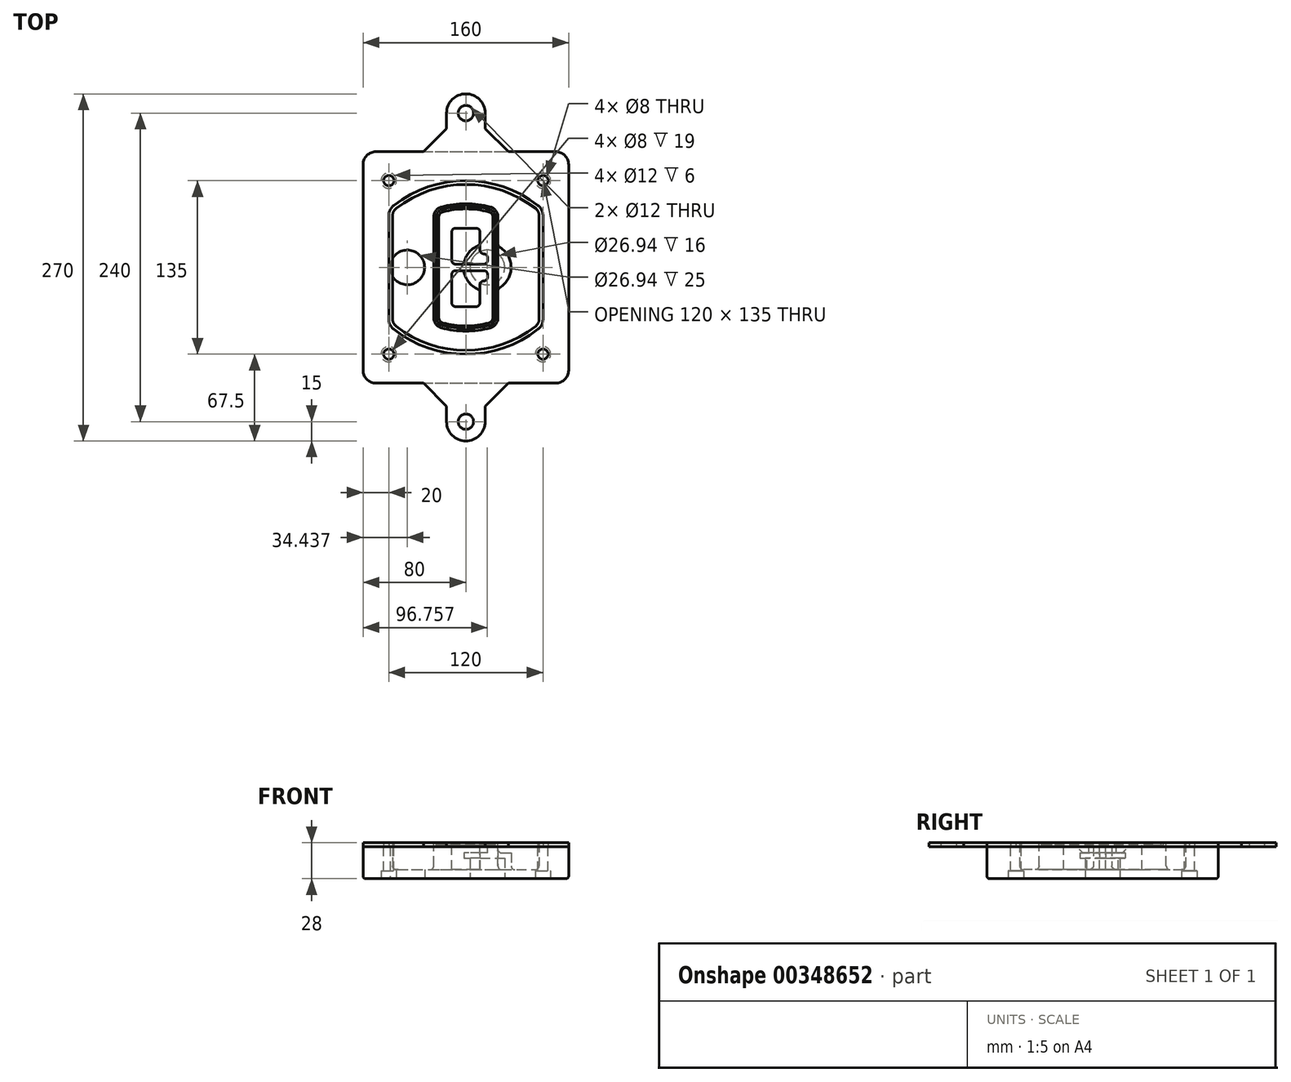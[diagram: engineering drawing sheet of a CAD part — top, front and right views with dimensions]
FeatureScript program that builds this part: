
annotation { "Feature Type Name" : "Feature", "Feature Type Description" : "" }
export const myFeature = defineFeature(function(context is Context, id is Id, definition is map)
    precondition{}
    {
        {
            var Q0;
            Q0=qCreatedBy(makeId("Top.planeOp"),FACE);
            var sketch = newSketch(context, id + "F0", { "sketchPlane" : qUnion([Q0])});
            skPoint(sketch, "E0.rect.middle", {"position": v(0, 0) * mm});
            skLineSegment(sketch, "E1.bottom", {"start": v(-70, -90) * mm, "end": v(70, -90) * mm});
            skLineSegment(sketch, "E1.top", {"start": v(-70, 90) * mm, "end": v(70, 90) * mm});
            skLineSegment(sketch, "E1.left", {"start": v(-80, -80) * mm, "end": v(-80, 80) * mm});
            skLineSegment(sketch, "E1.right", {"start": v(80, -80) * mm, "end": v(80, 80) * mm});
            skLineSegment(sketch, "E2", {"start": v(-80, 90) * mm, "end": v(80, -90) * mm, "construction": true});
            skLineSegment(sketch, "E3", {"start": v(80, 90) * mm, "end": v(-80, -90) * mm, "construction": true});
            skCircle(sketch, "E4", {"center": v(-60, 67.5) * mm, "radius": 4 * mm});
            skCircle(sketch, "E5", {"center": v(60, 67.5) * mm, "radius": 4 * mm});
            skCircle(sketch, "E6", {"center": v(60, -67.5) * mm, "radius": 4 * mm});
            skCircle(sketch, "E7", {"center": v(-60, -67.5) * mm, "radius": 4 * mm});
            skLineSegment(sketch, "E8", {"start": v(-60, 67.5) * mm, "end": v(60, 67.5) * mm, "construction": true});
            skLineSegment(sketch, "E9", {"start": v(60, 67.5) * mm, "end": v(60, -67.5) * mm, "construction": true});
            skLineSegment(sketch, "E10", {"start": v(60, -67.5) * mm, "end": v(-60, -67.5) * mm, "construction": true});
            skLineSegment(sketch, "E11", {"start": v(-60, -67.5) * mm, "end": v(-60, 67.5) * mm, "construction": true});
            skLineSegment(sketch, "E12", {"start": v(-60, 40.3) * mm, "end": v(-60, -40.3) * mm});
            skLineSegment(sketch, "E13", {"start": v(60, 40.3) * mm, "end": v(60, -40.3) * mm});
            skArc(sketch, "E14", {"start": v(56.15, 48.18) * mm, "mid": v(0, 67.5) * mm, "end": v(-56.15, 48.18) * mm});
            skArc(sketch, "E15", {"start": v(-56.15, -48.18) * mm, "mid": v(0, -67.5) * mm, "end": v(56.15, -48.18) * mm});
            skLineSegment(sketch, "E16", {"start": v(-60, 0) * mm, "end": v(60, 0) * mm, "construction": true});
            skPoint(sketch, "E17.visualSharp", {"position": v(-60, -45) * mm});
            skArc(sketch, "E17.filletArc", {"start": v(-60, -40.3) * mm, "mid": v(-58.99, -44.68) * mm, "end": v(-56.15, -48.18) * mm});
            skPoint(sketch, "E18.visualSharp", {"position": v(-60, 45) * mm});
            skArc(sketch, "E18.filletArc", {"start": v(-56.15, 48.18) * mm, "mid": v(-58.99, 44.68) * mm, "end": v(-60, 40.3) * mm});
            skPoint(sketch, "E19.visualSharp", {"position": v(60, 45) * mm});
            skArc(sketch, "E19.filletArc", {"start": v(60, 40.3) * mm, "mid": v(58.99, 44.68) * mm, "end": v(56.15, 48.18) * mm});
            skPoint(sketch, "E20.visualSharp", {"position": v(60, -45) * mm});
            skArc(sketch, "E20.filletArc", {"start": v(56.15, -48.18) * mm, "mid": v(58.99, -44.68) * mm, "end": v(60, -40.3) * mm});
            skPoint(sketch, "E21.visualSharp", {"position": v(-80, 90) * mm});
            skArc(sketch, "E21.filletArc", {"start": v(-70, 90) * mm, "mid": v(-77.07, 87.07) * mm, "end": v(-80, 80) * mm});
            skPoint(sketch, "E22.visualSharp", {"position": v(80, 90) * mm});
            skArc(sketch, "E22.filletArc", {"start": v(80, 80) * mm, "mid": v(77.07, 87.07) * mm, "end": v(70, 90) * mm});
            skPoint(sketch, "E23.visualSharp", {"position": v(80, -90) * mm});
            skArc(sketch, "E23.filletArc", {"start": v(70, -90) * mm, "mid": v(77.07, -87.07) * mm, "end": v(80, -80) * mm});
            skPoint(sketch, "E24.visualSharp", {"position": v(-80, -90) * mm});
            skArc(sketch, "E24.filletArc", {"start": v(-80, -80) * mm, "mid": v(-77.07, -87.07) * mm, "end": v(-70, -90) * mm});
            skArc(sketch, "E25.0", {"start": v(57, 40.3) * mm, "mid": v(56.3, 43.36) * mm, "end": v(54.3, 45.81) * mm});
            skLineSegment(sketch, "E25.1", {"start": v(57, 40.3) * mm, "end": v(57, -40.3) * mm});
            skArc(sketch, "E25.2", {"start": v(54.3, -45.81) * mm, "mid": v(56.3, -43.36) * mm, "end": v(57, -40.3) * mm});
            skArc(sketch, "E25.3", {"start": v(-54.3, -45.81) * mm, "mid": v(0, -64.5) * mm, "end": v(54.3, -45.81) * mm});
            skArc(sketch, "E25.4", {"start": v(-57, -40.3) * mm, "mid": v(-56.3, -43.36) * mm, "end": v(-54.3, -45.81) * mm});
            skArc(sketch, "E25.5", {"start": v(54.3, 45.81) * mm, "mid": v(0, 64.5) * mm, "end": v(-54.3, 45.81) * mm});
            skLineSegment(sketch, "E25.6", {"start": v(-57, 40.3) * mm, "end": v(-57, -40.3) * mm});
            skArc(sketch, "E25.7", {"start": v(-54.3, 45.81) * mm, "mid": v(-56.3, 43.36) * mm, "end": v(-57, 40.3) * mm});
            skArc(sketch, "E26.0", {"start": v(-58.62, 51.33) * mm, "mid": v(-62.58, 46.43) * mm, "end": v(-64, 40.3) * mm});
            skArc(sketch, "E26.1", {"start": v(58.62, 51.33) * mm, "mid": v(0, 71.5) * mm, "end": v(-58.62, 51.33) * mm});
            skArc(sketch, "E26.2", {"start": v(64, 40.3) * mm, "mid": v(62.58, 46.43) * mm, "end": v(58.62, 51.33) * mm});
            skLineSegment(sketch, "E26.3", {"start": v(64, 40.3) * mm, "end": v(64, -40.3) * mm});
            skArc(sketch, "E26.4", {"start": v(58.62, -51.33) * mm, "mid": v(62.58, -46.43) * mm, "end": v(64, -40.3) * mm});
            skLineSegment(sketch, "E26.5", {"start": v(-64, 40.3) * mm, "end": v(-64, -40.3) * mm});
            skArc(sketch, "E26.6", {"start": v(-58.62, -51.33) * mm, "mid": v(0, -71.5) * mm, "end": v(58.62, -51.33) * mm});
            skArc(sketch, "E26.7", {"start": v(-64, -40.3) * mm, "mid": v(-62.58, -46.43) * mm, "end": v(-58.62, -51.33) * mm});
            skSolve(sketch);
        }
        {
            var Q0;
            Q0=makeQuery(id+"F0.imprint","IMPRINT",FACE,{"disambiguationData":[TD([[makeQuery(id+"F0.imprint","IMPRINT",EDGE,{"derivedFrom":sQuery(id+"F0.wireOp",EDGE,"E1.bottom")}),1.0]])]});
            var Q1;
            Q1=makeQuery(id+"F0.imprint","IMPRINT",FACE,{"disambiguationData":[TD([[makeQuery(id+"F0.imprint","IMPRINT",EDGE,{"derivedFrom":sQuery(id+"F0.wireOp",EDGE,"E12")}),1.0]])]});
            var Q2;
            Q2=makeQuery(id+"F0.imprint","IMPRINT",FACE,{"disambiguationData":[TD([[makeQuery(id+"F0.imprint","IMPRINT",EDGE,{"derivedFrom":sQuery(id+"F0.wireOp",EDGE,"E25.0")}),1.0]])]});
            var Q3;
            Q3=makeQuery(id+"F0.imprint","IMPRINT",FACE,{"disambiguationData":[TD([[makeQuery(id+"F0.imprint","IMPRINT",EDGE,{"derivedFrom":sQuery(id+"F0.wireOp",EDGE,"E12")}),-1.0]])]});
            extrude(context, id + "F1", {"entities" : qUnion([Q0, Q1, Q2, Q3]), "oppositeDirection" : true, "depth" : 25 * mm});
        }
        {
            var Q0;
            Q0=makeQuery(id+"F0.imprint","IMPRINT",FACE,{"disambiguationData":[TD([[makeQuery(id+"F0.imprint","IMPRINT",EDGE,{"derivedFrom":sQuery(id+"F0.wireOp",EDGE,"E12")}),1.0]])]});
            extrude(context, id + "F2", {"entities" : qUnion([Q0]), "operationType" : NewBodyOperationType.ADD, "depth" : 3 * mm});
        }
        {
            var Q0;
            Q0=makeQuery(id+"F0.imprint","IMPRINT",FACE,{"disambiguationData":[TD([[makeQuery(id+"F0.imprint","IMPRINT",EDGE,{"derivedFrom":sQuery(id+"F0.wireOp",EDGE,"E25.0")}),1.0]])]});
            extrude(context, id + "F3", {"entities" : qUnion([Q0]), "operationType" : NewBodyOperationType.REMOVE, "oppositeDirection" : true, "depth" : 18 * mm});
        }
        {
            var Q0;
            Q0=makeQuery(id+"F2.opExtrude","CAP_FACE",FACE,{"disambiguationData":[OSD([sQuery(id+"F0.wireOp",EDGE,"E12"),sQuery(id+"F0.wireOp",EDGE,"E13"),sQuery(id+"F0.wireOp",EDGE,"E14"),sQuery(id+"F0.wireOp",EDGE,"E15"),sQuery(id+"F0.wireOp",EDGE,"E17.filletArc"),sQuery(id+"F0.wireOp",EDGE,"E18.filletArc"),sQuery(id+"F0.wireOp",EDGE,"E19.filletArc"),sQuery(id+"F0.wireOp",EDGE,"E20.filletArc"),sQuery(id+"F0.wireOp",EDGE,"E25.0"),sQuery(id+"F0.wireOp",EDGE,"E25.1"),sQuery(id+"F0.wireOp",EDGE,"E25.2"),sQuery(id+"F0.wireOp",EDGE,"E25.3"),sQuery(id+"F0.wireOp",EDGE,"E25.4"),sQuery(id+"F0.wireOp",EDGE,"E25.5"),sQuery(id+"F0.wireOp",EDGE,"E25.6"),sQuery(id+"F0.wireOp",EDGE,"E25.7")])],"isStart":false});
            var sketch = newSketch(context, id + "F4", { "sketchPlane" : qUnion([Q0])});
            skArc(sketch, "E27.0", {"start": v(-19.08, -46.97) * mm, "mid": v(0, -49.5) * mm, "end": v(19.08, -46.97) * mm});
            skArc(sketch, "E28.0", {"start": v(19.08, 46.97) * mm, "mid": v(0, 49.5) * mm, "end": v(-19.08, 46.97) * mm});
            skLineSegment(sketch, "E29", {"start": v(-25, 39.25) * mm, "end": v(-25, -39.25) * mm});
            skLineSegment(sketch, "E30", {"start": v(25, 39.25) * mm, "end": v(25, -39.25) * mm});
            skLineSegment(sketch, "E31", {"start": v(-25, 45.1) * mm, "end": v(25, 45.1) * mm, "construction": true});
            skLineSegment(sketch, "E32", {"start": v(-25, -45.1) * mm, "end": v(25, -45.1) * mm, "construction": true});
            skPoint(sketch, "E33.visualSharp", {"position": v(-25, 45.1) * mm});
            skArc(sketch, "E33.filletArc", {"start": v(-19.08, 46.97) * mm, "mid": v(-23.35, 44.11) * mm, "end": v(-25, 39.25) * mm});
            skPoint(sketch, "E34.visualSharp", {"position": v(25, 45.1) * mm});
            skArc(sketch, "E34.filletArc", {"start": v(25, 39.25) * mm, "mid": v(23.35, 44.11) * mm, "end": v(19.08, 46.97) * mm});
            skPoint(sketch, "E35.visualSharp", {"position": v(25, -45.1) * mm});
            skArc(sketch, "E35.filletArc", {"start": v(19.08, -46.97) * mm, "mid": v(23.35, -44.11) * mm, "end": v(25, -39.25) * mm});
            skPoint(sketch, "E36.visualSharp", {"position": v(-25, -45.1) * mm});
            skArc(sketch, "E36.filletArc", {"start": v(-25, -39.25) * mm, "mid": v(-23.35, -44.11) * mm, "end": v(-19.08, -46.97) * mm});
            skArc(sketch, "E37.0", {"start": v(54.3, 45.81) * mm, "mid": v(0, 64.5) * mm, "end": v(-54.3, 45.81) * mm});
            skArc(sketch, "E37.1", {"start": v(-54.3, 45.81) * mm, "mid": v(-56.3, 43.36) * mm, "end": v(-57, 40.3) * mm});
            skLineSegment(sketch, "E37.2", {"start": v(-57, 40.3) * mm, "end": v(-57, -40.3) * mm});
            skArc(sketch, "E37.3", {"start": v(-57, -40.3) * mm, "mid": v(-56.3, -43.36) * mm, "end": v(-54.3, -45.81) * mm});
            skArc(sketch, "E37.4", {"start": v(-54.3, -45.81) * mm, "mid": v(0, -64.5) * mm, "end": v(54.3, -45.81) * mm});
            skArc(sketch, "E37.5", {"start": v(54.3, -45.81) * mm, "mid": v(56.3, -43.36) * mm, "end": v(57, -40.3) * mm});
            skLineSegment(sketch, "E37.6", {"start": v(57, 40.3) * mm, "end": v(57, -40.3) * mm});
            skArc(sketch, "E37.7", {"start": v(57, 40.3) * mm, "mid": v(56.3, 43.36) * mm, "end": v(54.3, 45.81) * mm});
            skLineSegment(sketch, "E38.0", {"start": v(23, 39.25) * mm, "end": v(23, -39.25) * mm});
            skArc(sketch, "E38.1", {"start": v(18.56, -45.04) * mm, "mid": v(21.76, -42.9) * mm, "end": v(23, -39.25) * mm});
            skArc(sketch, "E38.2", {"start": v(-18.56, -45.04) * mm, "mid": v(0, -47.5) * mm, "end": v(18.56, -45.04) * mm});
            skArc(sketch, "E38.3", {"start": v(-23, -39.25) * mm, "mid": v(-21.76, -42.9) * mm, "end": v(-18.56, -45.04) * mm});
            skLineSegment(sketch, "E38.4", {"start": v(-23, 39.25) * mm, "end": v(-23, -39.25) * mm});
            skArc(sketch, "E38.5", {"start": v(23, 39.25) * mm, "mid": v(21.76, 42.9) * mm, "end": v(18.56, 45.04) * mm});
            skArc(sketch, "E38.6", {"start": v(-18.56, 45.04) * mm, "mid": v(-21.76, 42.9) * mm, "end": v(-23, 39.25) * mm});
            skArc(sketch, "E38.7", {"start": v(18.56, 45.04) * mm, "mid": v(0, 47.5) * mm, "end": v(-18.56, 45.04) * mm});
            skArc(sketch, "E39.0", {"start": v(21, 39.25) * mm, "mid": v(20.18, 41.68) * mm, "end": v(18.04, 43.1) * mm});
            skLineSegment(sketch, "E39.1", {"start": v(21, 39.25) * mm, "end": v(21, -39.25) * mm});
            skArc(sketch, "E39.2", {"start": v(18.04, -43.1) * mm, "mid": v(20.18, -41.68) * mm, "end": v(21, -39.25) * mm});
            skArc(sketch, "E39.3", {"start": v(-18.04, -43.1) * mm, "mid": v(0, -45.5) * mm, "end": v(18.04, -43.1) * mm});
            skArc(sketch, "E39.4", {"start": v(-21, -39.25) * mm, "mid": v(-20.18, -41.68) * mm, "end": v(-18.04, -43.1) * mm});
            skArc(sketch, "E39.5", {"start": v(18.04, 43.1) * mm, "mid": v(0, 45.5) * mm, "end": v(-18.04, 43.1) * mm});
            skLineSegment(sketch, "E39.6", {"start": v(-21, 39.25) * mm, "end": v(-21, -39.25) * mm});
            skArc(sketch, "E39.7", {"start": v(-18.04, 43.1) * mm, "mid": v(-20.18, 41.68) * mm, "end": v(-21, 39.25) * mm});
            skLineSegment(sketch, "E40", {"start": v(-25, 0) * mm, "end": v(25, 0) * mm, "construction": true});
            skLineSegment(sketch, "E41", {"start": v(-11, 5.5) * mm, "end": v(-11, 27.5) * mm});
            skLineSegment(sketch, "E42", {"start": v(-8, 30.5) * mm, "end": v(8, 30.5) * mm});
            skLineSegment(sketch, "E43", {"start": v(11, 27.5) * mm, "end": v(11, 13.5) * mm});
            skLineSegment(sketch, "E44", {"start": v(14, 10.5) * mm, "end": v(14, 10.5) * mm});
            skLineSegment(sketch, "E45", {"start": v(17, 7.5) * mm, "end": v(17, 5.5) * mm});
            skLineSegment(sketch, "E46", {"start": v(14, 2.5) * mm, "end": v(-8, 2.5) * mm});
            skPoint(sketch, "E47.visualSharp", {"position": v(-11, 30.5) * mm});
            skArc(sketch, "E47.filletArc", {"start": v(-8, 30.5) * mm, "mid": v(-10.12, 29.62) * mm, "end": v(-11, 27.5) * mm});
            skPoint(sketch, "E48.visualSharp", {"position": v(11, 30.5) * mm});
            skArc(sketch, "E48.filletArc", {"start": v(11, 27.5) * mm, "mid": v(10.12, 29.62) * mm, "end": v(8, 30.5) * mm});
            skPoint(sketch, "E49.visualSharp", {"position": v(11, 10.5) * mm});
            skArc(sketch, "E49.filletArc", {"start": v(11, 13.5) * mm, "mid": v(11.88, 11.38) * mm, "end": v(14, 10.5) * mm});
            skPoint(sketch, "E50.visualSharp", {"position": v(17, 10.5) * mm});
            skArc(sketch, "E50.filletArc", {"start": v(17, 7.5) * mm, "mid": v(16.12, 9.62) * mm, "end": v(14, 10.5) * mm});
            skPoint(sketch, "E51.visualSharp", {"position": v(17, 2.5) * mm});
            skArc(sketch, "E51.filletArc", {"start": v(14, 2.5) * mm, "mid": v(16.12, 3.38) * mm, "end": v(17, 5.5) * mm});
            skPoint(sketch, "E52.visualSharp", {"position": v(-11, 2.5) * mm});
            skArc(sketch, "E52.filletArc", {"start": v(-11, 5.5) * mm, "mid": v(-10.12, 3.38) * mm, "end": v(-8, 2.5) * mm});
            skLineSegment(sketch, "E53.0.MirrorCS", {"start": v(14, -2.5) * mm, "end": v(-8, -2.5) * mm});
            skArc(sketch, "E54.0.MirrorCS", {"start": v(-11, -5.5) * mm, "mid": v(-10.12, -3.38) * mm, "end": v(-8, -2.5) * mm});
            skLineSegment(sketch, "E55.0.MirrorCS", {"start": v(-11, -5.5) * mm, "end": v(-11, -27.5) * mm});
            skArc(sketch, "E56.0.MirrorCS", {"start": v(-8, -30.5) * mm, "mid": v(-10.12, -29.62) * mm, "end": v(-11, -27.5) * mm});
            skLineSegment(sketch, "E57.0.MirrorCS", {"start": v(-8, -30.5) * mm, "end": v(8, -30.5) * mm});
            skArc(sketch, "E58.0.MirrorCS", {"start": v(11, -27.5) * mm, "mid": v(10.12, -29.62) * mm, "end": v(8, -30.5) * mm});
            skLineSegment(sketch, "E59.0.MirrorCS", {"start": v(11, -27.5) * mm, "end": v(11, -13.5) * mm});
            skArc(sketch, "E60.0.MirrorCS", {"start": v(11, -13.5) * mm, "mid": v(11.88, -11.38) * mm, "end": v(14, -10.5) * mm});
            skArc(sketch, "E61.0.MirrorCS", {"start": v(17, -7.5) * mm, "mid": v(16.12, -9.62) * mm, "end": v(14, -10.5) * mm});
            skLineSegment(sketch, "E62.0.MirrorCS", {"start": v(17, -7.5) * mm, "end": v(17, -5.5) * mm});
            skArc(sketch, "E63.0.MirrorCS", {"start": v(14, -2.5) * mm, "mid": v(16.12, -3.38) * mm, "end": v(17, -5.5) * mm});
            skSolve(sketch);
        }
        {
            var Q0;
            Q0=makeQuery(id+"F4.imprint","IMPRINT",FACE,{"disambiguationData":[TD([[makeQuery(id+"F4.imprint","IMPRINT",EDGE,{"derivedFrom":sQuery(id+"F4.wireOp",EDGE,"E27.0")}),1.0]])]});
            var Q1;
            Q1=makeQuery(id+"F4.imprint","IMPRINT",FACE,{"disambiguationData":[TD([[makeQuery(id+"F4.imprint","IMPRINT",EDGE,{"derivedFrom":sQuery(id+"F4.wireOp",EDGE,"E38.0")}),-1.0]])]});
            var Q2;
            Q2=makeQuery(id+"F4.imprint","IMPRINT",FACE,{"disambiguationData":[TD([[makeQuery(id+"F4.imprint","IMPRINT",EDGE,{"derivedFrom":sQuery(id+"F4.wireOp",EDGE,"E39.0")}),1.0]])]});
            extrude(context, id + "F5", {"entities" : qUnion([Q0, Q1, Q2]), "operationType" : NewBodyOperationType.ADD, "endBound" : BoundingType.UP_TO_NEXT, "oppositeDirection" : true, "depth" : 25 * mm});
        }
        {
            var Q0;
            Q0=makeQuery(id+"F4.imprint","IMPRINT",FACE,{"disambiguationData":[TD([[makeQuery(id+"F4.imprint","IMPRINT",EDGE,{"derivedFrom":sQuery(id+"F4.wireOp",EDGE,"E38.0")}),-1.0]])]});
            extrude(context, id + "F6", {"entities" : qUnion([Q0]), "operationType" : NewBodyOperationType.REMOVE, "oppositeDirection" : true, "depth" : 2 * mm});
        }
        {
            var Q0;
            Q0=makeQuery(id+"F1.opExtrude","CAP_FACE",FACE,{"disambiguationData":[OSD([sQuery(id+"F0.wireOp",EDGE,"E1.bottom"),sQuery(id+"F0.wireOp",EDGE,"E1.top"),sQuery(id+"F0.wireOp",EDGE,"E1.left"),sQuery(id+"F0.wireOp",EDGE,"E1.right"),sQuery(id+"F0.wireOp",EDGE,"E4"),sQuery(id+"F0.wireOp",EDGE,"E5"),sQuery(id+"F0.wireOp",EDGE,"E6"),sQuery(id+"F0.wireOp",EDGE,"E7"),sQuery(id+"F0.wireOp",EDGE,"E21.filletArc"),sQuery(id+"F0.wireOp",EDGE,"E22.filletArc"),sQuery(id+"F0.wireOp",EDGE,"E23.filletArc"),sQuery(id+"F0.wireOp",EDGE,"E24.filletArc")])],"isStart":false});
            var sketch = newSketch(context, id + "F7", { "sketchPlane" : qUnion([Q0])});
            skCircle(sketch, "E64", {"center": v(16.76, 0) * mm, "radius": 13.47 * mm});
            skCircle(sketch, "E65", {"center": v(-45.56, 0) * mm, "radius": 13.47 * mm});
            skLineSegment(sketch, "E66", {"start": v(80, 0) * mm, "end": v(-80, 0) * mm});
            skCircle(sketch, "E67", {"center": v(16.76, 0) * mm, "radius": 18.47 * mm});
            skCircle(sketch, "E68", {"center": v(60, -67.5) * mm, "radius": 6 * mm});
            skCircle(sketch, "E69", {"center": v(-60, -67.5) * mm, "radius": 6 * mm});
            skCircle(sketch, "E70", {"center": v(-60, 67.5) * mm, "radius": 6 * mm});
            skCircle(sketch, "E71", {"center": v(60, 67.5) * mm, "radius": 6 * mm});
            skSolve(sketch);
        }
        {
            var Q0;
            {var subQ1=sQuery(id+"F7.wireOp",EDGE,"E66");var subQ4=sQuery(id+"F7.wireOp",EDGE,"E64");var subQ6=makeQuery(id+"F7.imprint","INTERSECT",VERTEX,{"disambiguationData":[OD(0.0)],"derivedFrom":[subQ4,subQ1]});Q0=makeQuery(id+"F7.imprint","IMPRINT",FACE,{"disambiguationData":[TD([[makeQuery(id+"F7.imprint","IMPRINT",EDGE,{"disambiguationData":[TD([[subQ6,-1.0]])],"derivedFrom":subQ4}),-1.0]])]});}
            var Q1;
            {var subQ0=sQuery(id+"F7.wireOp",EDGE,"E66");var subQ1=sQuery(id+"F7.wireOp",EDGE,"E64");var subQ3=makeQuery(id+"F7.imprint","INTERSECT",VERTEX,{"disambiguationData":[OD(0.0)],"derivedFrom":[subQ1,subQ0]});Q1=makeQuery(id+"F7.imprint","IMPRINT",FACE,{"disambiguationData":[TD([[makeQuery(id+"F7.imprint","IMPRINT",EDGE,{"disambiguationData":[TD([[subQ3,-1.0]])],"derivedFrom":subQ1}),1.0]])]});}
            var Q2;
            {var subQ0=sQuery(id+"F7.wireOp",EDGE,"E66");var subQ1=sQuery(id+"F7.wireOp",EDGE,"E64");var subQ3=makeQuery(id+"F7.imprint","INTERSECT",VERTEX,{"disambiguationData":[OD(0.0)],"derivedFrom":[subQ1,subQ0]});Q2=makeQuery(id+"F7.imprint","IMPRINT",FACE,{"disambiguationData":[TD([[makeQuery(id+"F7.imprint","IMPRINT",EDGE,{"disambiguationData":[TD([[subQ3,1.0]])],"derivedFrom":subQ1}),1.0]])]});}
            var Q3;
            {var subQ1=sQuery(id+"F7.wireOp",EDGE,"E66");var subQ4=sQuery(id+"F7.wireOp",EDGE,"E64");var subQ6=makeQuery(id+"F7.imprint","INTERSECT",VERTEX,{"disambiguationData":[OD(0.0)],"derivedFrom":[subQ4,subQ1]});Q3=makeQuery(id+"F7.imprint","IMPRINT",FACE,{"disambiguationData":[TD([[makeQuery(id+"F7.imprint","IMPRINT",EDGE,{"disambiguationData":[TD([[subQ6,1.0]])],"derivedFrom":subQ4}),-1.0]])]});}
            extrude(context, id + "F8", {"entities" : qUnion([Q0, Q1, Q2, Q3]), "operationType" : NewBodyOperationType.ADD, "oppositeDirection" : true, "depth" : 20 * mm});
        }
        {
            var Q0;
            {var subQ0=sQuery(id+"F7.wireOp",EDGE,"E66");var subQ1=sQuery(id+"F7.wireOp",EDGE,"E64");var subQ3=makeQuery(id+"F7.imprint","INTERSECT",VERTEX,{"disambiguationData":[OD(0.0)],"derivedFrom":[subQ1,subQ0]});Q0=makeQuery(id+"F7.imprint","IMPRINT",FACE,{"disambiguationData":[TD([[makeQuery(id+"F7.imprint","IMPRINT",EDGE,{"disambiguationData":[TD([[subQ3,-1.0]])],"derivedFrom":subQ1}),1.0]])]});}
            var Q1;
            {var subQ0=sQuery(id+"F7.wireOp",EDGE,"E66");var subQ1=sQuery(id+"F7.wireOp",EDGE,"E64");var subQ3=makeQuery(id+"F7.imprint","INTERSECT",VERTEX,{"disambiguationData":[OD(0.0)],"derivedFrom":[subQ1,subQ0]});Q1=makeQuery(id+"F7.imprint","IMPRINT",FACE,{"disambiguationData":[TD([[makeQuery(id+"F7.imprint","IMPRINT",EDGE,{"disambiguationData":[TD([[subQ3,1.0]])],"derivedFrom":subQ1}),1.0]])]});}
            extrude(context, id + "F9", {"entities" : qUnion([Q0, Q1]), "operationType" : NewBodyOperationType.REMOVE, "oppositeDirection" : true, "depth" : 16 * mm});
        }
        {
            var Q0;
            {var subQ0=sQuery(id+"F7.wireOp",EDGE,"E66");var subQ1=sQuery(id+"F7.wireOp",EDGE,"E65");var subQ3=makeQuery(id+"F7.imprint","INTERSECT",VERTEX,{"disambiguationData":[OD(0.0)],"derivedFrom":[subQ1,subQ0]});Q0=makeQuery(id+"F7.imprint","IMPRINT",FACE,{"disambiguationData":[TD([[makeQuery(id+"F7.imprint","IMPRINT",EDGE,{"disambiguationData":[TD([[subQ3,-1.0]])],"derivedFrom":subQ1}),1.0]])]});}
            var Q1;
            {var subQ0=sQuery(id+"F7.wireOp",EDGE,"E66");var subQ1=sQuery(id+"F7.wireOp",EDGE,"E65");var subQ3=makeQuery(id+"F7.imprint","INTERSECT",VERTEX,{"disambiguationData":[OD(0.0)],"derivedFrom":[subQ1,subQ0]});Q1=makeQuery(id+"F7.imprint","IMPRINT",FACE,{"disambiguationData":[TD([[makeQuery(id+"F7.imprint","IMPRINT",EDGE,{"disambiguationData":[TD([[subQ3,1.0]])],"derivedFrom":subQ1}),1.0]])]});}
            extrude(context, id + "F10", {"entities" : qUnion([Q0, Q1]), "operationType" : NewBodyOperationType.REMOVE, "oppositeDirection" : true, "depth" : 25 * mm});
        }
        {
            var Q0;
            Q0=makeQuery(id+"F7.imprint","IMPRINT",FACE,{"disambiguationData":[TD([[makeQuery(id+"F7.imprint","IMPRINT",EDGE,{"derivedFrom":sQuery(id+"F7.wireOp",EDGE,"E68")}),1.0]])]});
            var Q1;
            Q1=makeQuery(id+"F7.imprint","IMPRINT",FACE,{"disambiguationData":[TD([[makeQuery(id+"F7.imprint","IMPRINT",EDGE,{"derivedFrom":makeQuery(id+"F1.opExtrude","CAP_EDGE",EDGE,{"disambiguationData":[OSD([sQuery(id+"F0.wireOp",EDGE,"E5")])],"isStart":false})}),-1.0]])]});
            var Q2;
            Q2=makeQuery(id+"F7.imprint","IMPRINT",FACE,{"disambiguationData":[TD([[makeQuery(id+"F7.imprint","IMPRINT",EDGE,{"derivedFrom":sQuery(id+"F7.wireOp",EDGE,"E69")}),1.0]])]});
            var Q3;
            Q3=makeQuery(id+"F7.imprint","IMPRINT",FACE,{"disambiguationData":[TD([[makeQuery(id+"F7.imprint","IMPRINT",EDGE,{"derivedFrom":makeQuery(id+"F1.opExtrude","CAP_EDGE",EDGE,{"disambiguationData":[OSD([sQuery(id+"F0.wireOp",EDGE,"E4")])],"isStart":false})}),-1.0]])]});
            var Q4;
            Q4=makeQuery(id+"F7.imprint","IMPRINT",FACE,{"disambiguationData":[TD([[makeQuery(id+"F7.imprint","IMPRINT",EDGE,{"derivedFrom":sQuery(id+"F7.wireOp",EDGE,"E70")}),1.0]])]});
            var Q5;
            Q5=makeQuery(id+"F7.imprint","IMPRINT",FACE,{"disambiguationData":[TD([[makeQuery(id+"F7.imprint","IMPRINT",EDGE,{"derivedFrom":makeQuery(id+"F1.opExtrude","CAP_EDGE",EDGE,{"disambiguationData":[OSD([sQuery(id+"F0.wireOp",EDGE,"E7")])],"isStart":false})}),-1.0]])]});
            var Q6;
            Q6=makeQuery(id+"F7.imprint","IMPRINT",FACE,{"disambiguationData":[TD([[makeQuery(id+"F7.imprint","IMPRINT",EDGE,{"derivedFrom":sQuery(id+"F7.wireOp",EDGE,"E71")}),1.0]])]});
            var Q7;
            Q7=makeQuery(id+"F7.imprint","IMPRINT",FACE,{"disambiguationData":[TD([[makeQuery(id+"F7.imprint","IMPRINT",EDGE,{"derivedFrom":makeQuery(id+"F1.opExtrude","CAP_EDGE",EDGE,{"disambiguationData":[OSD([sQuery(id+"F0.wireOp",EDGE,"E6")])],"isStart":false})}),-1.0]])]});
            extrude(context, id + "F11", {"entities" : qUnion([Q0, Q1, Q2, Q3, Q4, Q5, Q6, Q7]), "operationType" : NewBodyOperationType.REMOVE, "oppositeDirection" : true, "depth" : 6 * mm});
        }
        {
            var Q0;
            Q0=makeQuery(id+"F9.boolean.opBoolean","COPY",FACE,{"derivedFrom":makeQuery(id+"F9.opExtrude","CAP_FACE",FACE,{"disambiguationData":[OSD([sQuery(id+"F7.wireOp",EDGE,"E64")])],"isStart":false})});
            var sketch = newSketch(context, id + "F12", { "sketchPlane" : qUnion([Q0])});
            skArc(sketch, "E72.0", {"start": v(11, 17.55) * mm, "mid": v(2.57, 11.82) * mm, "end": v(-1.54, 2.5) * mm});
            skArc(sketch, "E72.1", {"start": v(-1.54, -2.5) * mm, "mid": v(2.57, -11.82) * mm, "end": v(11, -17.55) * mm});
            skLineSegment(sketch, "E73", {"start": v(-1.54, -2.5) * mm, "end": v(14, -2.5) * mm});
            skLineSegment(sketch, "E74.0", {"start": v(14, 2.5) * mm, "end": v(-1.54, 2.5) * mm});
            skArc(sketch, "E74.1", {"start": v(14, 2.5) * mm, "mid": v(16.12, 3.38) * mm, "end": v(17, 5.5) * mm});
            skLineSegment(sketch, "E74.2", {"start": v(17, 7.5) * mm, "end": v(17, 5.5) * mm});
            skArc(sketch, "E74.3", {"start": v(17, 7.5) * mm, "mid": v(16.12, 9.62) * mm, "end": v(14, 10.5) * mm});
            skArc(sketch, "E74.4", {"start": v(11, 13.5) * mm, "mid": v(11.88, 11.38) * mm, "end": v(14, 10.5) * mm});
            skLineSegment(sketch, "E74.5", {"start": v(11, 17.55) * mm, "end": v(11, 13.5) * mm});
            skLineSegment(sketch, "E74.7", {"start": v(14, -2.5) * mm, "end": v(-1.54, -2.5) * mm});
            skArc(sketch, "E74.8", {"start": v(14, -2.5) * mm, "mid": v(16.12, -3.38) * mm, "end": v(17, -5.5) * mm});
            skLineSegment(sketch, "E74.9", {"start": v(17, -7.5) * mm, "end": v(17, -5.5) * mm});
            skArc(sketch, "E74.10", {"start": v(17, -7.5) * mm, "mid": v(16.12, -9.62) * mm, "end": v(14, -10.5) * mm});
            skArc(sketch, "E74.11", {"start": v(11, -13.5) * mm, "mid": v(11.88, -11.38) * mm, "end": v(14, -10.5) * mm});
            skLineSegment(sketch, "E74.12", {"start": v(11, -17.55) * mm, "end": v(11, -13.5) * mm});
            skPoint(sketch, "E75.orphan", {"position": v(11, -27.5) * mm});
            skPoint(sketch, "E76.orphan", {"position": v(-8, -2.5) * mm});
            skPoint(sketch, "E77.orphan", {"position": v(-8, 2.5) * mm});
            skPoint(sketch, "E78.orphan", {"position": v(11, 27.5) * mm});
            skSolve(sketch);
        }
        {
            var Q0;
            {var subQ7=sQuery(id+"F12.wireOp",EDGE,"E72.0");var subQ14=sQuery(id+"F12.wireOp",EDGE,"E72.1");var subQ16=sQuery(id+"F12.wireOp",EDGE,"E74.1");var subQ18=sQuery(id+"F12.wireOp",EDGE,"E74.8");Q0=qUnion([makeQuery(id+"F12.imprint","IMPRINT",FACE,{"disambiguationData":[TD([[makeQuery(id+"F12.imprint","IMPRINT",EDGE,{"derivedFrom":subQ7}),1.0]])]}),makeQuery(id+"F12.imprint","IMPRINT",FACE,{"disambiguationData":[TD([[makeQuery(id+"F12.imprint","IMPRINT",EDGE,{"derivedFrom":subQ14}),1.0]])]}),makeQuery(id+"F12.imprint","IMPRINT",FACE,{"disambiguationData":[TD([[makeQuery(id+"F12.imprint","IMPRINT",EDGE,{"derivedFrom":subQ16}),1.0]])]}),makeQuery(id+"F12.imprint","IMPRINT",FACE,{"disambiguationData":[TD([[makeQuery(id+"F12.imprint","IMPRINT",EDGE,{"derivedFrom":subQ18}),-1.0]])]})]);}
            var Q1;
            Q1=makeQuery(id+"F5.boolean.opBoolean","SPLIT",FACE,{"disambiguationData":[TD([makeQuery(id+"F5.opExtrude","SWEPT_FACE",FACE,{"disambiguationData":[OSD([sQuery(id+"F4.wireOp",EDGE,"E41")])]})])],"derivedFrom":makeQuery(id+"F3.boolean.opBoolean","COPY",FACE,{"derivedFrom":makeQuery(id+"F3.opExtrude","CAP_FACE",FACE,{"disambiguationData":[OSD([sQuery(id+"F0.wireOp",EDGE,"E25.0"),sQuery(id+"F0.wireOp",EDGE,"E25.1"),sQuery(id+"F0.wireOp",EDGE,"E25.2"),sQuery(id+"F0.wireOp",EDGE,"E25.3"),sQuery(id+"F0.wireOp",EDGE,"E25.4"),sQuery(id+"F0.wireOp",EDGE,"E25.5"),sQuery(id+"F0.wireOp",EDGE,"E25.6"),sQuery(id+"F0.wireOp",EDGE,"E25.7")])],"isStart":false})})});
            extrude(context, id + "F13", {"entities" : qUnion([Q0]), "operationType" : NewBodyOperationType.REMOVE, "endBound" : BoundingType.UP_TO_SURFACE, "endBoundEntityFace" : qUnion([Q1]), "depth" : 25 * mm});
        }
        {
            var Q0;
            Q0=makeQuery(id+"F3.boolean.opBoolean","COPY",EDGE,{"derivedFrom":makeQuery(id+"F3.opExtrude","CAP_EDGE",EDGE,{"disambiguationData":[OSD([sQuery(id+"F0.wireOp",EDGE,"E25.6")])],"isStart":false})});
            var Q1;
            Q1=makeQuery(id+"F8.boolean.opBoolean","INTERSECT",EDGE,{"derivedFrom":[makeQuery(id+"F5.opExtrude","SWEPT_FACE",FACE,{"disambiguationData":[OSD([sQuery(id+"F4.wireOp",EDGE,"E30")])]}),makeQuery(id+"F8.opExtrude","CAP_FACE",FACE,{"disambiguationData":[OSD([sQuery(id+"F7.wireOp",EDGE,"E67")])],"isStart":false})]});
            var Q2;
            Q2=makeQuery(id+"F8.boolean.opBoolean","INTERSECT",EDGE,{"disambiguationData":[OD(1.0)],"derivedFrom":[makeQuery(id+"F5.opExtrude","SWEPT_FACE",FACE,{"disambiguationData":[OSD([sQuery(id+"F4.wireOp",EDGE,"E30")])]}),makeQuery(id+"F8.opExtrude","SWEPT_FACE",FACE,{"disambiguationData":[OSD([sQuery(id+"F7.wireOp",EDGE,"E67")])]})]});
            var Q3;
            {var subQ0=sQuery(id+"F4.wireOp",EDGE,"E30");Q3=makeQuery(id+"F8.boolean.opBoolean","SPLIT",EDGE,{"disambiguationData":[TD([makeQuery(id+"F5.opExtrude","SWEPT_FACE",FACE,{"disambiguationData":[OSD([sQuery(id+"F4.wireOp",EDGE,"E35.filletArc")])]})])],"derivedFrom":makeQuery(id+"F5.opExtrude","CAP_EDGE",EDGE,{"disambiguationData":[OSD([subQ0])],"isStart":false})});}
            var Q4;
            {var subQ0=sQuery(id+"F0.wireOp",EDGE,"E25.7");var subQ1=sQuery(id+"F0.wireOp",EDGE,"E25.1");var subQ2=sQuery(id+"F0.wireOp",EDGE,"E25.6");var subQ3=sQuery(id+"F0.wireOp",EDGE,"E25.5");var subQ4=sQuery(id+"F0.wireOp",EDGE,"E25.4");var subQ5=sQuery(id+"F0.wireOp",EDGE,"E25.0");var subQ6=sQuery(id+"F0.wireOp",EDGE,"E25.2");var subQ7=sQuery(id+"F0.wireOp",EDGE,"E25.3");Q4=makeQuery(id+"F8.boolean.opBoolean","INTERSECT",EDGE,{"derivedFrom":[makeQuery(id+"F5.boolean.opBoolean","SPLIT",FACE,{"disambiguationData":[TD([makeQuery(id+"F2.opExtrude","SWEPT_FACE",FACE,{"disambiguationData":[OSD([subQ5])]})])],"derivedFrom":makeQuery(id+"F3.boolean.opBoolean","COPY",FACE,{"derivedFrom":makeQuery(id+"F3.opExtrude","CAP_FACE",FACE,{"disambiguationData":[OSD([subQ5,subQ1,subQ6,subQ7,subQ4,subQ3,subQ2,subQ0])],"isStart":false})})}),makeQuery(id+"F8.opExtrude","SWEPT_FACE",FACE,{"disambiguationData":[OSD([sQuery(id+"F7.wireOp",EDGE,"E67")])]})]});}
            var Q5;
            Q5=makeQuery(id+"F8.boolean.opBoolean","INTERSECT",EDGE,{"disambiguationData":[OD(0.0)],"derivedFrom":[makeQuery(id+"F5.opExtrude","SWEPT_FACE",FACE,{"disambiguationData":[OSD([sQuery(id+"F4.wireOp",EDGE,"E30")])]}),makeQuery(id+"F8.opExtrude","SWEPT_FACE",FACE,{"disambiguationData":[OSD([sQuery(id+"F7.wireOp",EDGE,"E67")])]})]});
            fillet(context, id + "F14", {"entities" : qUnion([Q0, Q1, Q2, Q3, Q4, Q5]), "radius" : 3 * mm, "tangentPropagation" : true, "allowEdgeOverflow" : false});
        }
        {
            var Q0;
            Q0=makeQuery(id+"F1.opExtrude","CAP_EDGE",EDGE,{"disambiguationData":[OSD([sQuery(id+"F0.wireOp",EDGE,"E1.bottom")])],"isStart":false});
            fillet(context, id + "F15", {"entities" : qUnion([Q0]), "radius" : 2 * mm, "tangentPropagation" : true, "allowEdgeOverflow" : false});
        }
        {
            var Q0;
            {var subQ0=sQuery(id+"F0.wireOp",EDGE,"E21.filletArc");var subQ1=sQuery(id+"F0.wireOp",EDGE,"E7");var subQ2=sQuery(id+"F0.wireOp",EDGE,"E6");var subQ3=sQuery(id+"F0.wireOp",EDGE,"E5");var subQ4=sQuery(id+"F0.wireOp",EDGE,"E4");var subQ5=sQuery(id+"F0.wireOp",EDGE,"E22.filletArc");var subQ6=sQuery(id+"F0.wireOp",EDGE,"E1.bottom");var subQ7=sQuery(id+"F0.wireOp",EDGE,"E1.right");var subQ8=sQuery(id+"F0.wireOp",EDGE,"E1.top");var subQ9=sQuery(id+"F0.wireOp",EDGE,"E1.left");var subQ10=sQuery(id+"F0.wireOp",EDGE,"E23.filletArc");var subQ11=sQuery(id+"F0.wireOp",EDGE,"E24.filletArc");Q0=makeQuery(id+"F2.boolean.opBoolean","SPLIT",FACE,{"disambiguationData":[TD([makeQuery(id+"F1.opExtrude","SWEPT_FACE",FACE,{"disambiguationData":[OSD([subQ6])]})])],"derivedFrom":makeQuery(id+"F1.opExtrude","CAP_FACE",FACE,{"disambiguationData":[OSD([subQ6,subQ8,subQ9,subQ7,subQ4,subQ3,subQ2,subQ1,subQ0,subQ5,subQ10,subQ11])],"isStart":true})});}
            var sketch = newSketch(context, id + "F16", { "sketchPlane" : qUnion([Q0])});
            skCircle(sketch, "E79.0", {"center": v(-60, 67.5) * mm, "radius": 4 * mm});
            skCircle(sketch, "E80.0", {"center": v(60, 67.5) * mm, "radius": 4 * mm});
            skLineSegment(sketch, "E81.0.0", {"start": v(70, 90) * mm, "end": v(-70, 90) * mm});
            skArc(sketch, "E81.0.1", {"start": v(-70, 90) * mm, "mid": v(-77.07, 87.07) * mm, "end": v(-80, 80) * mm});
            skLineSegment(sketch, "E81.0.2", {"start": v(-80, 80) * mm, "end": v(-80, -80) * mm});
            skArc(sketch, "E81.0.3", {"start": v(-80, -80) * mm, "mid": v(-77.07, -87.07) * mm, "end": v(-70, -90) * mm});
            skLineSegment(sketch, "E81.0.4", {"start": v(-70, -90) * mm, "end": v(70, -90) * mm});
            skArc(sketch, "E81.0.5", {"start": v(70, -90) * mm, "mid": v(77.07, -87.07) * mm, "end": v(80, -80) * mm});
            skLineSegment(sketch, "E81.0.6", {"start": v(80, -80) * mm, "end": v(80, 80) * mm});
            skArc(sketch, "E81.0.7", {"start": v(80, 80) * mm, "mid": v(77.07, 87.07) * mm, "end": v(70, 90) * mm});
            skCircle(sketch, "E82.0", {"center": v(-60, -67.5) * mm, "radius": 4 * mm});
            skCircle(sketch, "E83.0", {"center": v(60, -67.5) * mm, "radius": 4 * mm});
            skLineSegment(sketch, "E84", {"start": v(0, 90) * mm, "end": v(0, 120) * mm, "construction": true});
            skCircle(sketch, "E85", {"center": v(0, 120) * mm, "radius": 6 * mm});
            skArc(sketch, "E86", {"start": v(15, 120) * mm, "mid": v(0, 135) * mm, "end": v(-15, 120) * mm});
            skLineSegment(sketch, "E87", {"start": v(-15, 120) * mm, "end": v(-15, 108) * mm});
            skLineSegment(sketch, "E88", {"start": v(-15, 108) * mm, "end": v(-33, 90) * mm});
            skLineSegment(sketch, "E89", {"start": v(15, 120) * mm, "end": v(15, 108) * mm});
            skLineSegment(sketch, "E90", {"start": v(15, 108) * mm, "end": v(33, 90) * mm});
            skLineSegment(sketch, "E91", {"start": v(-80, 0) * mm, "end": v(80, 0) * mm, "construction": true});
            skLineSegment(sketch, "E92.MirrorCS", {"start": v(-15, -108) * mm, "end": v(-33, -90) * mm});
            skLineSegment(sketch, "E93.MirrorCS", {"start": v(15, -120) * mm, "end": v(15, -108) * mm});
            skArc(sketch, "E94.MirrorCS", {"start": v(15, -120) * mm, "mid": v(0, -135) * mm, "end": v(-15, -120) * mm});
            skCircle(sketch, "E95.MirrorC", {"center": v(0, -120) * mm, "radius": 6 * mm});
            skLineSegment(sketch, "E96.MirrorCS", {"start": v(-15, -120) * mm, "end": v(-15, -108) * mm});
            skLineSegment(sketch, "E97.MirrorCS", {"start": v(0, -90) * mm, "end": v(0, -120) * mm, "construction": true});
            skLineSegment(sketch, "E98.MirrorCS", {"start": v(15, -108) * mm, "end": v(33, -90) * mm});
            skSolve(sketch);
        }
        {
            var Q0;
            Q0=makeQuery(id+"F16.imprint","IMPRINT",FACE,{"disambiguationData":[TD([[makeQuery(id+"F16.imprint","IMPRINT",EDGE,{"derivedFrom":sQuery(id+"F16.wireOp",EDGE,"E85")}),-1.0]])]});
            var Q1;
            Q1=makeQuery(id+"F16.imprint","IMPRINT",FACE,{"disambiguationData":[TD([[makeQuery(id+"F16.imprint","IMPRINT",EDGE,{"derivedFrom":sQuery(id+"F16.wireOp",EDGE,"E79.0")}),-1.0]])]});
            var Q2;
            {var subQ0=sQuery(id+"F16.wireOp",EDGE,"E92.MirrorCS");Q2=makeQuery(id+"F16.imprint","IMPRINT",FACE,{"disambiguationData":[TD([[makeQuery(id+"F16.imprint","IMPRINT",EDGE,{"derivedFrom":subQ0}),-1.0]])]});}
            var Q3;
            Q3=makeQuery(id+"F2.opExtrude","CAP_FACE",FACE,{"disambiguationData":[OSD([sQuery(id+"F0.wireOp",EDGE,"E12"),sQuery(id+"F0.wireOp",EDGE,"E13"),sQuery(id+"F0.wireOp",EDGE,"E14"),sQuery(id+"F0.wireOp",EDGE,"E15"),sQuery(id+"F0.wireOp",EDGE,"E17.filletArc"),sQuery(id+"F0.wireOp",EDGE,"E18.filletArc"),sQuery(id+"F0.wireOp",EDGE,"E19.filletArc"),sQuery(id+"F0.wireOp",EDGE,"E20.filletArc"),sQuery(id+"F0.wireOp",EDGE,"E25.0"),sQuery(id+"F0.wireOp",EDGE,"E25.1"),sQuery(id+"F0.wireOp",EDGE,"E25.2"),sQuery(id+"F0.wireOp",EDGE,"E25.3"),sQuery(id+"F0.wireOp",EDGE,"E25.4"),sQuery(id+"F0.wireOp",EDGE,"E25.5"),sQuery(id+"F0.wireOp",EDGE,"E25.6"),sQuery(id+"F0.wireOp",EDGE,"E25.7")])],"isStart":false});
            extrude(context, id + "F17", {"entities" : qUnion([Q0, Q1, Q2]), "endBound" : BoundingType.UP_TO_SURFACE, "endBoundEntityFace" : qUnion([Q3]), "depth" : 25 * mm});
        }
    });
